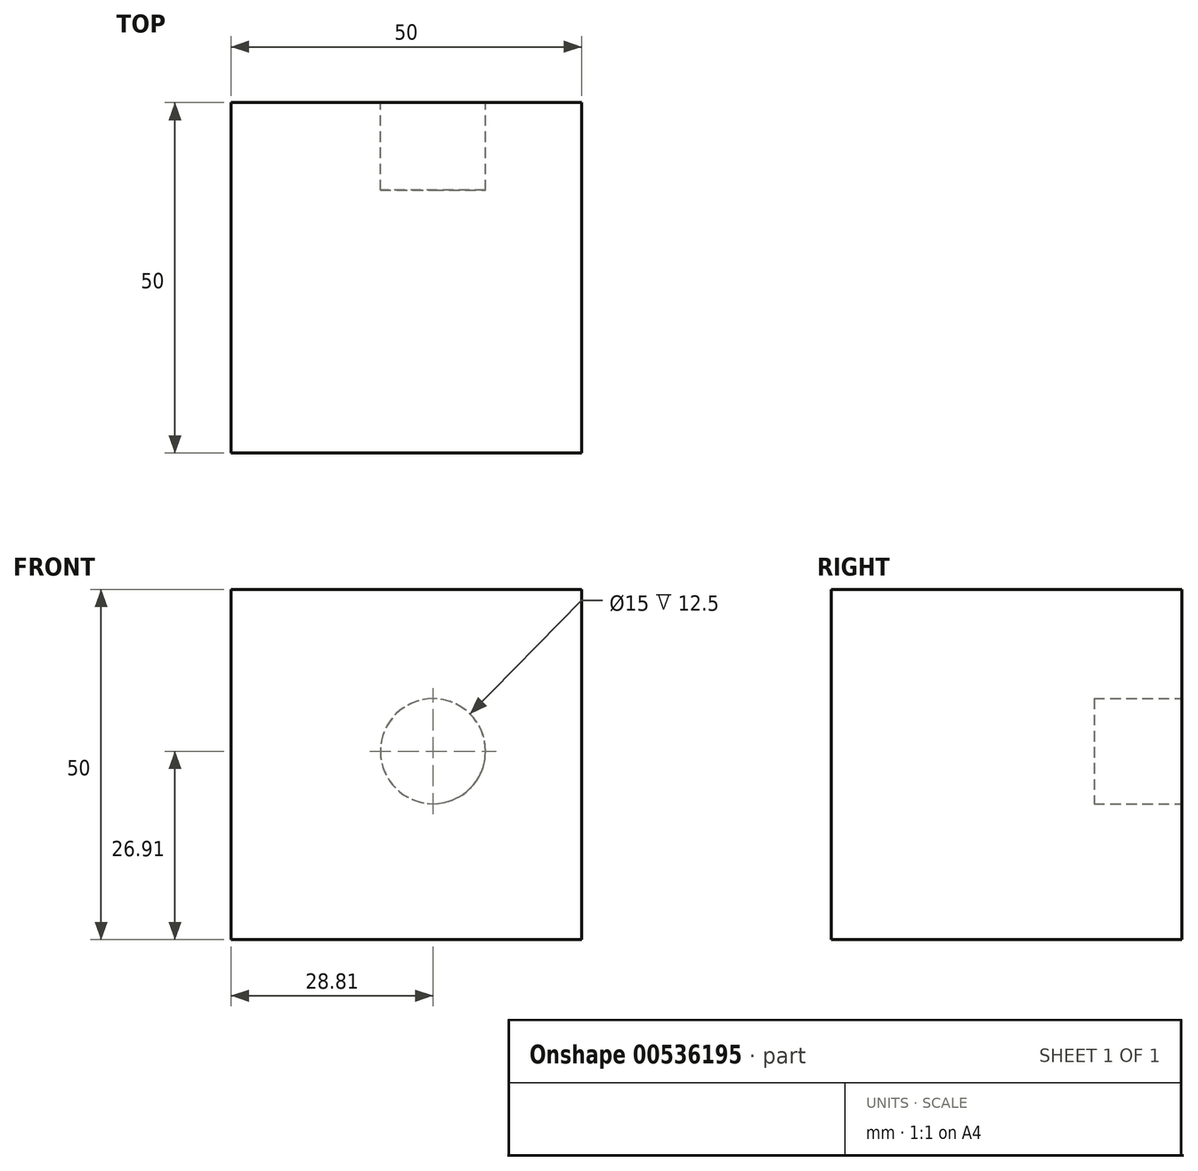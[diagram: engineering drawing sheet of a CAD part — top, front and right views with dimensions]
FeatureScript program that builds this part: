
annotation { "Feature Type Name" : "Feature", "Feature Type Description" : "" }
export const myFeature = defineFeature(function(context is Context, id is Id, definition is map)
    precondition{}
    {
        {
            var Q0;
            Q0=qCreatedBy(makeId("Front.planeOp"),FACE);
            var sketch = newSketch(context, id + "F0", { "sketchPlane" : qUnion([Q0])});
            skLineSegment(sketch, "E0.bottom", {"start": v(-28.81, 23.1) * mm, "end": v(21.19, 23.1) * mm});
            skLineSegment(sketch, "E0.top", {"start": v(-28.81, -26.9) * mm, "end": v(21.19, -26.9) * mm});
            skLineSegment(sketch, "E0.left", {"start": v(-28.81, 23.1) * mm, "end": v(-28.81, -26.9) * mm});
            skLineSegment(sketch, "E0.right", {"start": v(21.19, 23.1) * mm, "end": v(21.19, -26.9) * mm});
            skSolve(sketch);
        }
        {
            var Q0;
            Q0=makeQuery(id+"F0.imprint","IMPRINT",FACE,{"disambiguationData":[TD([[makeQuery(id+"F0.imprint","IMPRINT",EDGE,{"derivedFrom":sQuery(id+"F0.wireOp",EDGE,"E0.bottom")}),-1.0]])]});
            var Q1;
            Q1 = qConstructionFilter(qBodyType(qCreatedBy(id + "F0" ,EDGE), BodyType.WIRE), ConstructionObject.NO);
            var Q2;
            Q2 = qConstructionFilter(qBodyType(qCreatedBy(id + "F2" ,EDGE), BodyType.WIRE), ConstructionObject.NO);
            extrude(context, id + "F1", {"entities" : qUnion([Q0]), "surfaceEntities" : qUnion([Q1, Q2]), "oppositeDirection" : true, "depth" : 50 * mm, "offsetDistance" : 25 * mm});
        }
        {
            var Q0;
            Q0=makeQuery(id+"F1.opExtrude","CAP_FACE",FACE,{"disambiguationData":[OSD([sQuery(id+"F0.wireOp",EDGE,"E0.bottom"),sQuery(id+"F0.wireOp",EDGE,"E0.top"),sQuery(id+"F0.wireOp",EDGE,"E0.left"),sQuery(id+"F0.wireOp",EDGE,"E0.right")])],"isStart":false});
            var sketch = newSketch(context, id + "F2", { "sketchPlane" : qUnion([Q0])});
            skCircle(sketch, "E1", {"center": v(0, 0) * mm, "radius": 7.5 * mm});
            skSolve(sketch);
        }
        {
            var Q0;
            Q0=makeQuery(id+"F2.imprint","IMPRINT",FACE,{"disambiguationData":[TD([[makeQuery(id+"F2.imprint","IMPRINT",EDGE,{"derivedFrom":sQuery(id+"F2.wireOp",EDGE,"E1")}),1.0]])]});
            var Q1;
            Q1=sQuery(id+"F2.wireOp",EDGE,"E1");
            extrude(context, id + "F3", {"entities" : qUnion([Q0]), "operationType" : NewBodyOperationType.REMOVE, "surfaceEntities" : qUnion([Q1]), "endBound" : BoundingType.SYMMETRIC, "oppositeDirection" : true, "depth" : 25 * mm, "offsetDistance" : 25 * mm});
        }
    });
